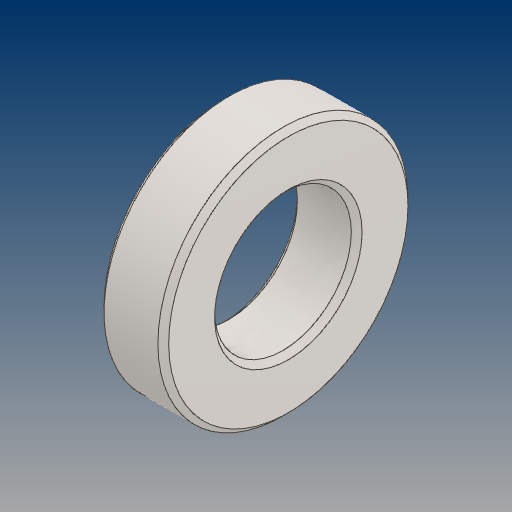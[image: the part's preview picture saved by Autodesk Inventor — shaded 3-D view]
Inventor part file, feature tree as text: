
AUTODESK INVENTOR PART (.ipt)
format: ipt  version: 2021 (Build 250183000, 183)  size: 124,416 bytes
history: native  units: mm
features: chamfer x1
ambient origin geometry x8: Origin, YZ Plane, XZ Plane, XY Plane, X Axis, Y Axis, Z Axis, Center Point
bodies: Solid1 (feature_tree)
feature tree (1):
  chamfer  "Chamfer1"  [1 undecoded]
note: 1 required parameter value undecoded (feature->parameter linkage not recoverable at this tier; creation-order binding heuristic only, values carry confidence <= 0.55)
